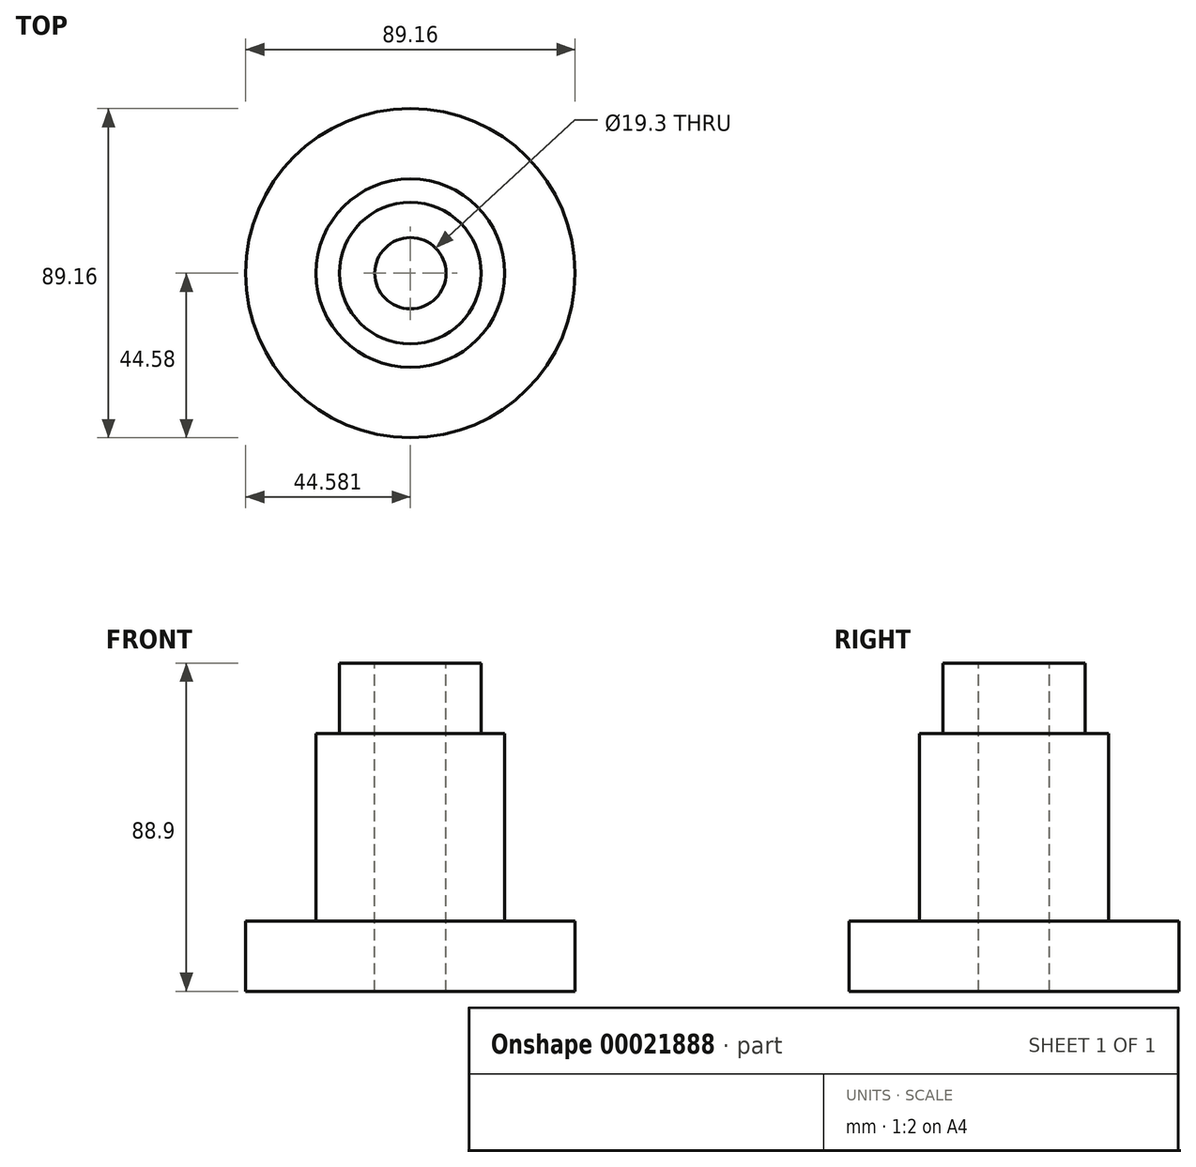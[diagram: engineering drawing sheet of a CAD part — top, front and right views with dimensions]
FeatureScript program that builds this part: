
annotation { "Feature Type Name" : "Feature", "Feature Type Description" : "" }
export const myFeature = defineFeature(function(context is Context, id is Id, definition is map)
    precondition{}
    {
        {
            var Q0;
            Q0=qCreatedBy(makeId("Front.planeOp"),FACE);
            var sketch = newSketch(context, id + "F0", { "sketchPlane" : qUnion([Q0])});
            skLineSegment(sketch, "E0", {"start": v(-28.43, 66.57) * mm, "end": v(-28.43, -22.33) * mm});
            skLineSegment(sketch, "E1", {"start": v(-28.43, -22.33) * mm, "end": v(6.5, -22.33) * mm});
            skLineSegment(sketch, "E2", {"start": v(6.5, -22.33) * mm, "end": v(6.5, -3.28) * mm});
            skLineSegment(sketch, "E3", {"start": v(6.5, -3.28) * mm, "end": v(-12.55, -3.28) * mm});
            skLineSegment(sketch, "E4", {"start": v(-12.55, -3.28) * mm, "end": v(-12.55, 47.52) * mm});
            skLineSegment(sketch, "E5", {"start": v(-12.55, 47.52) * mm, "end": v(-18.9, 47.52) * mm});
            skLineSegment(sketch, "E6", {"start": v(-18.9, 47.52) * mm, "end": v(-18.9, 59.15) * mm});
            skLineSegment(sketch, "E7", {"start": v(-18.9, 59.15) * mm, "end": v(-18.9, 59.15) * mm});
            skLineSegment(sketch, "E8", {"start": v(-18.9, 59.15) * mm, "end": v(-18.9, 66.57) * mm});
            skLineSegment(sketch, "E9", {"start": v(-18.9, 66.57) * mm, "end": v(-28.43, 66.57) * mm});
            skLineSegment(sketch, "E10", {"start": v(-38.08, 66.42) * mm, "end": v(-38.08, -22.48) * mm});
            skSolve(sketch);
        }
        {
            var Q0;
            Q0=makeQuery(id+"F0.imprint","IMPRINT",FACE,{"disambiguationData":[TD([[makeQuery(id+"F0.imprint","IMPRINT",EDGE,{"derivedFrom":sQuery(id+"F0.wireOp",EDGE,"E0")}),1.0]])]});
            var Q1;
            Q1=sQuery(id+"F0.wireOp",EDGE,"E10");
            revolve(context, id + "F1", {"entities" : qUnion([Q0]), "axis" : qUnion([Q1]), "revolveType" : RevolveType.FULL});
        }
    });
